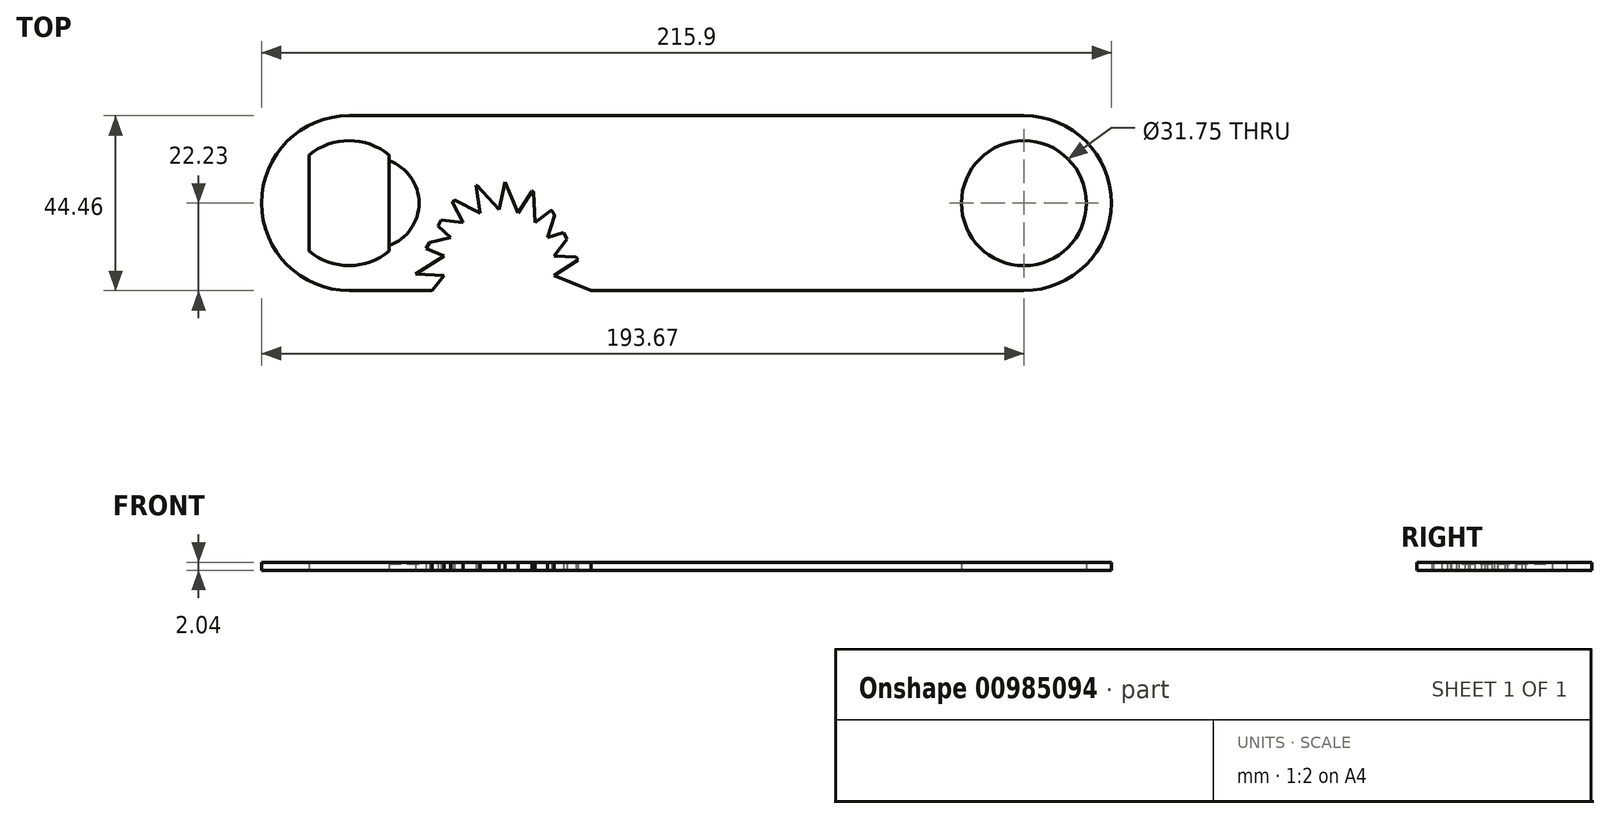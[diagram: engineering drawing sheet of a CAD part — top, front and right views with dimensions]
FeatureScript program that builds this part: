
annotation { "Feature Type Name" : "Feature", "Feature Type Description" : "" }
export const myFeature = defineFeature(function(context is Context, id is Id, definition is map)
    precondition{}
    {
        {
            var Q0;
            Q0=qCreatedBy(makeId("Top.planeOp"),FACE);
            var sketch = newSketch(context, id + "F0", { "sketchPlane" : qUnion([Q0])});
            skLineSegment(sketch, "E0.bottom", {"start": v(-95.25, 22.22) * mm, "end": v(76.2, 22.22) * mm});
            skLineSegment(sketch, "E0.top", {"start": v(-95.25, -22.23) * mm, "end": v(-77.64, -22.23) * mm});
            skArc(sketch, "E1", {"start": v(-95.25, 22.22) * mm, "mid": v(-117.48, 0) * mm, "end": v(-95.25, -22.23) * mm});
            skArc(sketch, "E2", {"start": v(76.2, -22.23) * mm, "mid": v(98.43, 0) * mm, "end": v(76.2, 22.22) * mm});
            skCircle(sketch, "E3", {"center": v(76.2, 0) * mm, "radius": 15.88 * mm});
            skArc(sketch, "E4", {"start": v(-85.1, 12.2) * mm, "mid": v(-95.25, 15.87) * mm, "end": v(-105.4, 12.2) * mm});
            skLineSegment(sketch, "E5", {"start": v(-105.41, -12.2) * mm, "end": v(-105.41, 12.2) * mm});
            skLineSegment(sketch, "E6", {"start": v(-85.1, -12.2) * mm, "end": v(-85.1, 12.2) * mm});
            skArc(sketch, "E7.trimOffspring", {"start": v(-105.41, -12.2) * mm, "mid": v(-95.25, -15.88) * mm, "end": v(-85.1, -12.2) * mm});
            skLineSegment(sketch, "E8", {"start": v(-77.64, -22.23) * mm, "end": v(-68.42, -4.5) * mm, "construction": true});
            skLineSegment(sketch, "E9", {"start": v(-48.23, 0) * mm, "end": v(-48.22, -0.02) * mm});
            skCircle(sketch, "E10", {"center": v(-57.15, -15.88) * mm, "radius": 15.24 * mm, "construction": true});
            skPoint(sketch, "E11.orphan", {"position": v(-57.15, 17.13) * mm});
            skLineSegment(sketch, "E12.trimOffspring", {"start": v(-36.66, -22.23) * mm, "end": v(76.2, -22.23) * mm});
            skLineSegment(sketch, "E13", {"start": v(-57.15, -0.64) * mm, "end": v(-57.15, 5.71) * mm, "construction": true});
            skLineSegment(sketch, "E14", {"start": v(-57.15, -1.65) * mm, "end": v(-64.4, 6.27) * mm});
            skLineSegment(sketch, "E15", {"start": v(-64.4, 6.27) * mm, "end": v(-54.83, 8.83) * mm});
            skLineSegment(sketch, "E16", {"start": v(-54.83, 8.83) * mm, "end": v(-57.15, -1.65) * mm});
            skLineSegment(sketch, "E17", {"start": v(-57.15, -1.65) * mm, "end": v(-59.62, 7.55) * mm, "construction": true});
            skLineSegment(sketch, "E18.1.0", {"start": v(-63.42, 8.14) * mm, "end": v(-62.01, -2.5) * mm});
            skLineSegment(sketch, "E18.1.1", {"start": v(-62.01, -2.5) * mm, "end": v(-71.54, 2.45) * mm});
            skLineSegment(sketch, "E18.1.2", {"start": v(-71.54, 2.45) * mm, "end": v(-63.42, 8.14) * mm});
            skLineSegment(sketch, "E18.2.0", {"start": v(-71.25, 4.55) * mm, "end": v(-66.3, -4.98) * mm});
            skLineSegment(sketch, "E18.2.1", {"start": v(-66.3, -4.98) * mm, "end": v(-76.94, -3.58) * mm});
            skLineSegment(sketch, "E18.2.2", {"start": v(-76.94, -3.58) * mm, "end": v(-71.25, 4.55) * mm});
            skLineSegment(sketch, "E18.3.0", {"start": v(-77.39, -1.5) * mm, "end": v(-69.47, -8.76) * mm});
            skLineSegment(sketch, "E18.3.1", {"start": v(-69.47, -8.76) * mm, "end": v(-79.95, -11.09) * mm});
            skLineSegment(sketch, "E18.3.2", {"start": v(-79.95, -11.09) * mm, "end": v(-77.39, -1.5) * mm});
            skLineSegment(sketch, "E18.4.0", {"start": v(-81.08, -9.3) * mm, "end": v(-71.16, -13.4) * mm});
            skLineSegment(sketch, "E18.4.1", {"start": v(-71.16, -13.4) * mm, "end": v(-80.21, -19.17) * mm});
            skLineSegment(sketch, "E18.4.2", {"start": v(-80.21, -19.17) * mm, "end": v(-81.08, -9.3) * mm});
            skLineSegment(sketch, "E18.5.0", {"start": v(-81.89, -17.88) * mm, "end": v(-71.16, -18.34) * mm});
            skLineSegment(sketch, "E18.5.1", {"start": v(-71.16, -18.34) * mm, "end": v(-74.14, -22.23) * mm});
            skLineSegment(sketch, "E18.5.2", {"start": v(-79.86, -22.23) * mm, "end": v(-81.89, -17.88) * mm});
            skLineSegment(sketch, "E19.2.13.0", {"start": v(-33.77, -22.23) * mm, "end": v(-43.14, -18.34) * mm});
            skLineSegment(sketch, "E19.3.13.0", {"start": v(-43.14, -18.34) * mm, "end": v(-34.09, -12.58) * mm});
            skLineSegment(sketch, "E19.6.13.0", {"start": v(-34.09, -12.58) * mm, "end": v(-33.24, -22.23) * mm});
            skLineSegment(sketch, "E19.2.14.0", {"start": v(-32.41, -13.87) * mm, "end": v(-43.14, -13.4) * mm});
            skLineSegment(sketch, "E19.3.14.0", {"start": v(-43.14, -13.4) * mm, "end": v(-36.6, -4.89) * mm});
            skLineSegment(sketch, "E19.6.14.0", {"start": v(-36.6, -4.89) * mm, "end": v(-32.41, -13.87) * mm});
            skLineSegment(sketch, "E19.2.15.0", {"start": v(-34.6, -5.53) * mm, "end": v(-44.83, -8.76) * mm});
            skLineSegment(sketch, "E19.3.15.0", {"start": v(-44.83, -8.76) * mm, "end": v(-41.6, 1.48) * mm});
            skLineSegment(sketch, "E19.6.15.0", {"start": v(-41.6, 1.48) * mm, "end": v(-34.6, -5.53) * mm});
            skLineSegment(sketch, "E19.2.16.0", {"start": v(-39.49, 1.56) * mm, "end": v(-48, -4.98) * mm});
            skLineSegment(sketch, "E19.3.16.0", {"start": v(-48, -4.98) * mm, "end": v(-48.48, 5.75) * mm});
            skLineSegment(sketch, "E19.6.16.0", {"start": v(-48.48, 5.75) * mm, "end": v(-39.49, 1.56) * mm});
            skLineSegment(sketch, "E19.2.17.0", {"start": v(-46.52, 6.55) * mm, "end": v(-52.29, -2.5) * mm});
            skLineSegment(sketch, "E19.3.17.0", {"start": v(-52.29, -2.5) * mm, "end": v(-56.4, 7.41) * mm});
            skLineSegment(sketch, "E19.6.17.0", {"start": v(-56.4, 7.41) * mm, "end": v(-46.52, 6.55) * mm});
            skLineSegment(sketch, "E20", {"start": v(-36.66, -22.23) * mm, "end": v(-33.77, -22.23) * mm});
            skPoint(sketch, "E21.orphan", {"position": v(-33.22, -22.45) * mm});
            skLineSegment(sketch, "E22", {"start": v(-74.14, -22.23) * mm, "end": v(-77.64, -22.23) * mm});
            skArc(sketch, "E23", {"start": v(-45.88, -4.5) * mm, "mid": v(-57.15, 2.33) * mm, "end": v(-68.42, -4.5) * mm, "construction": true});
            skLineSegment(sketch, "E24.trimOffspring", {"start": v(-66.23, -0.31) * mm, "end": v(-66.07, 0) * mm});
            skLineSegment(sketch, "E25.trimOffspring", {"start": v(-45.88, -4.5) * mm, "end": v(-36.66, -22.23) * mm, "construction": true});
            skLineSegment(sketch, "E26.0", {"start": v(-43.07, -3.04) * mm, "end": v(-33.08, -22.23) * mm});
            skArc(sketch, "E26.1", {"start": v(-43.07, -3.04) * mm, "mid": v(-57.15, 5.5) * mm, "end": v(-71.23, -3.04) * mm});
            skLineSegment(sketch, "E26.2", {"start": v(-81.22, -22.23) * mm, "end": v(-71.23, -3.04) * mm});
            skPoint(sketch, "E27", {"position": v(-117.48, 0) * mm});
            skCircle(sketch, "E28", {"center": v(-57.15, -15.88) * mm, "radius": 14.22 * mm, "construction": true});
            skSolve(sketch);
        }
        {
            var Q0;
            Q0=makeQuery(id+"F0.imprint","IMPRINT",FACE,{"disambiguationData":[TD([[makeQuery(id+"F0.imprint","IMPRINT",EDGE,{"derivedFrom":sQuery(id+"F0.wireOp",EDGE,"E0.bottom")}),-1.0]])]});
            var Q1;
            {var subQ0=sQuery(id+"F0.wireOp",EDGE,"E18.4.1");var subQ1=sQuery(id+"F0.wireOp",EDGE,"E8");var subQ2=makeQuery(id+"F0.imprint","INTERSECT",VERTEX,{"derivedFrom":[subQ1,subQ0]});Q1=makeQuery(id+"F0.imprint","IMPRINT",FACE,{"disambiguationData":[TD([[makeQuery(id+"F0.imprint","IMPRINT",EDGE,{"disambiguationData":[TD([[subQ2,-1.0]])],"derivedFrom":subQ1}),1.0]])]});}
            var Q2;
            {var subQ0=sQuery(id+"F0.wireOp",EDGE,"E18.5.0");var subQ1=sQuery(id+"F0.wireOp",EDGE,"E18.4.1");var subQ2=makeQuery(id+"F0.imprint","INTERSECT",VERTEX,{"derivedFrom":[subQ1,subQ0]});Q2=makeQuery(id+"F0.imprint","IMPRINT",FACE,{"disambiguationData":[TD([[makeQuery(id+"F0.imprint","IMPRINT",EDGE,{"disambiguationData":[TD([[subQ2,-1.0]])],"derivedFrom":subQ1}),-1.0]])]});}
            var Q3;
            {var subQ0=sQuery(id+"F0.wireOp",EDGE,"E18.3.1");var subQ1=sQuery(id+"F0.wireOp",EDGE,"E8");var subQ2=makeQuery(id+"F0.imprint","INTERSECT",VERTEX,{"derivedFrom":[subQ1,subQ0]});Q3=makeQuery(id+"F0.imprint","IMPRINT",FACE,{"disambiguationData":[TD([[makeQuery(id+"F0.imprint","IMPRINT",EDGE,{"disambiguationData":[TD([[subQ2,-1.0]])],"derivedFrom":subQ1}),1.0]])]});}
            var Q4;
            {var subQ0=sQuery(id+"F0.wireOp",EDGE,"E18.2.1");var subQ1=sQuery(id+"F0.wireOp",EDGE,"E8");var subQ2=makeQuery(id+"F0.imprint","INTERSECT",VERTEX,{"derivedFrom":[subQ1,subQ0]});Q4=makeQuery(id+"F0.imprint","IMPRINT",FACE,{"disambiguationData":[TD([[makeQuery(id+"F0.imprint","IMPRINT",EDGE,{"disambiguationData":[TD([[subQ2,-1.0]])],"derivedFrom":subQ1}),1.0]])]});}
            var Q5;
            {var subQ0=sQuery(id+"F0.wireOp",EDGE,"E18.3.0");var subQ1=sQuery(id+"F0.wireOp",EDGE,"E18.2.1");var subQ2=makeQuery(id+"F0.imprint","INTERSECT",VERTEX,{"derivedFrom":[subQ1,subQ0]});Q5=makeQuery(id+"F0.imprint","IMPRINT",FACE,{"disambiguationData":[TD([[makeQuery(id+"F0.imprint","IMPRINT",EDGE,{"disambiguationData":[TD([[subQ2,-1.0]])],"derivedFrom":subQ1}),-1.0]])]});}
            var Q6;
            {var subQ0=sQuery(id+"F0.wireOp",EDGE,"E18.2.0");var subQ1=sQuery(id+"F0.wireOp",EDGE,"E18.1.1");var subQ2=makeQuery(id+"F0.imprint","INTERSECT",VERTEX,{"derivedFrom":[subQ1,subQ0]});Q6=makeQuery(id+"F0.imprint","IMPRINT",FACE,{"disambiguationData":[TD([[makeQuery(id+"F0.imprint","IMPRINT",EDGE,{"disambiguationData":[TD([[subQ2,-1.0]])],"derivedFrom":subQ1}),-1.0]])]});}
            var Q7;
            {var subQ1=sQuery(id+"F0.wireOp",EDGE,"E18.1.1");var subQ7=sQuery(id+"F0.wireOp",EDGE,"PH1tnpYM-GYzg-ddA6-vLUi-DHPLtai6QRXg");var subQ8=makeQuery(id+"F0.imprint","INTERSECT",VERTEX,{"derivedFrom":[subQ7,subQ1]});Q7=makeQuery(id+"F0.imprint","IMPRINT",FACE,{"disambiguationData":[TD([[makeQuery(id+"F0.imprint","IMPRINT",EDGE,{"disambiguationData":[TD([[subQ8,1.0]])],"derivedFrom":subQ7}),-1.0]])]});}
            var Q8;
            {var subQ0=sQuery(id+"F0.wireOp",EDGE,"E18.1.1");var subQ1=sQuery(id+"F0.wireOp",EDGE,"PH1tnpYM-GYzg-ddA6-vLUi-DHPLtai6QRXg");var subQ2=makeQuery(id+"F0.imprint","INTERSECT",VERTEX,{"derivedFrom":[subQ1,subQ0]});Q8=makeQuery(id+"F0.imprint","IMPRINT",FACE,{"disambiguationData":[TD([[makeQuery(id+"F0.imprint","IMPRINT",EDGE,{"disambiguationData":[TD([[subQ2,1.0]])],"derivedFrom":subQ1}),1.0]])]});}
            var Q9;
            {var subQ0=sQuery(id+"F0.wireOp",EDGE,"E18.2.1");var subQ1=sQuery(id+"F0.wireOp",EDGE,"E8");var subQ2=makeQuery(id+"F0.imprint","INTERSECT",VERTEX,{"derivedFrom":[subQ1,subQ0]});Q9=makeQuery(id+"F0.imprint","IMPRINT",FACE,{"disambiguationData":[TD([[makeQuery(id+"F0.imprint","IMPRINT",EDGE,{"disambiguationData":[TD([[subQ2,-1.0]])],"derivedFrom":subQ1}),-1.0]])]});}
            var Q10;
            {var subQ0=sQuery(id+"F0.wireOp",EDGE,"E18.3.1");var subQ1=sQuery(id+"F0.wireOp",EDGE,"E8");var subQ2=makeQuery(id+"F0.imprint","INTERSECT",VERTEX,{"derivedFrom":[subQ1,subQ0]});Q10=makeQuery(id+"F0.imprint","IMPRINT",FACE,{"disambiguationData":[TD([[makeQuery(id+"F0.imprint","IMPRINT",EDGE,{"disambiguationData":[TD([[subQ2,-1.0]])],"derivedFrom":subQ1}),-1.0]])]});}
            var Q11;
            {var subQ0=sQuery(id+"F0.wireOp",EDGE,"E18.4.1");var subQ1=sQuery(id+"F0.wireOp",EDGE,"E8");var subQ2=makeQuery(id+"F0.imprint","INTERSECT",VERTEX,{"derivedFrom":[subQ1,subQ0]});Q11=makeQuery(id+"F0.imprint","IMPRINT",FACE,{"disambiguationData":[TD([[makeQuery(id+"F0.imprint","IMPRINT",EDGE,{"disambiguationData":[TD([[subQ2,-1.0]])],"derivedFrom":subQ1}),-1.0]])]});}
            var Q12;
            {var subQ0=sQuery(id+"F0.wireOp",EDGE,"E18.5.1");var subQ1=sQuery(id+"F0.wireOp",EDGE,"E8");var subQ2=makeQuery(id+"F0.imprint","INTERSECT",VERTEX,{"derivedFrom":[subQ1,subQ0]});Q12=makeQuery(id+"F0.imprint","IMPRINT",FACE,{"disambiguationData":[TD([[makeQuery(id+"F0.imprint","IMPRINT",EDGE,{"disambiguationData":[TD([[subQ2,-1.0]])],"derivedFrom":subQ1}),-1.0]])]});}
            var Q13;
            {var subQ0=sQuery(id+"F0.wireOp",EDGE,"E16");var subQ1=sQuery(id+"F0.wireOp",EDGE,"PH1tnpYM-GYzg-ddA6-vLUi-DHPLtai6QRXg");var subQ2=makeQuery(id+"F0.imprint","INTERSECT",VERTEX,{"derivedFrom":[subQ1,subQ0]});Q13=makeQuery(id+"F0.imprint","IMPRINT",FACE,{"disambiguationData":[TD([[makeQuery(id+"F0.imprint","IMPRINT",EDGE,{"disambiguationData":[TD([[subQ2,-1.0]])],"derivedFrom":subQ1}),1.0]])]});}
            var Q14;
            {var subQ0=sQuery(id+"F0.wireOp",EDGE,"E16");var subQ1=sQuery(id+"F0.wireOp",EDGE,"PH1tnpYM-GYzg-ddA6-vLUi-DHPLtai6QRXg");var subQ2=makeQuery(id+"F0.imprint","INTERSECT",VERTEX,{"derivedFrom":[subQ1,subQ0]});Q14=makeQuery(id+"F0.imprint","IMPRINT",FACE,{"disambiguationData":[TD([[makeQuery(id+"F0.imprint","IMPRINT",EDGE,{"disambiguationData":[TD([[subQ2,-1.0]])],"derivedFrom":subQ1}),-1.0]])]});}
            var Q15;
            {var subQ0=sQuery(id+"F0.wireOp",EDGE,"E18.1.0");var subQ1=sQuery(id+"F0.wireOp",EDGE,"PH1tnpYM-GYzg-ddA6-vLUi-DHPLtai6QRXg");var subQ2=makeQuery(id+"F0.imprint","INTERSECT",VERTEX,{"derivedFrom":[subQ1,subQ0]});Q15=makeQuery(id+"F0.imprint","IMPRINT",FACE,{"disambiguationData":[TD([[makeQuery(id+"F0.imprint","IMPRINT",EDGE,{"disambiguationData":[TD([[subQ2,-1.0]])],"derivedFrom":subQ1}),-1.0]])]});}
            var Q16;
            {var subQ0=sQuery(id+"F0.wireOp",EDGE,"E16");var subQ1=sQuery(id+"F0.wireOp",EDGE,"E15");var subQ2=makeQuery(id+"F0.imprint","INTERSECT",VERTEX,{"derivedFrom":[subQ1,subQ0]});Q16=makeQuery(id+"F0.imprint","IMPRINT",FACE,{"disambiguationData":[TD([[makeQuery(id+"F0.imprint","IMPRINT",EDGE,{"disambiguationData":[TD([[subQ2,1.0]])],"derivedFrom":subQ1}),-1.0]])]});}
            var Q17;
            {var subQ12=sQuery(id+"F0.wireOp",EDGE,"PH1tnpYM-GYzg-ddA6-vLUi-DHPLtai6QRXg");var subQ13=sQuery(id+"F0.wireOp",EDGE,"E9");var subQ14=makeQuery(id+"F0.imprint","INTERSECT",VERTEX,{"derivedFrom":[subQ13,subQ12]});Q17=makeQuery(id+"F0.imprint","IMPRINT",FACE,{"disambiguationData":[TD([[makeQuery(id+"F0.imprint","IMPRINT",EDGE,{"disambiguationData":[TD([[subQ14,-1.0]])],"derivedFrom":subQ13}),1.0]])]});}
            var Q18;
            {var subQ0=sQuery(id+"F0.wireOp",EDGE,"E19.2.17.0");var subQ1=sQuery(id+"F0.wireOp",EDGE,"E19.3.16.0");var subQ2=makeQuery(id+"F0.imprint","INTERSECT",VERTEX,{"derivedFrom":[subQ1,subQ0]});Q18=makeQuery(id+"F0.imprint","IMPRINT",FACE,{"disambiguationData":[TD([[makeQuery(id+"F0.imprint","IMPRINT",EDGE,{"disambiguationData":[TD([[subQ2,-1.0]])],"derivedFrom":subQ1}),-1.0]])]});}
            var Q19;
            {var subQ0=sQuery(id+"F0.wireOp",EDGE,"E19.3.15.0");var subQ1=sQuery(id+"F0.wireOp",EDGE,"E9");var subQ2=makeQuery(id+"F0.imprint","INTERSECT",VERTEX,{"derivedFrom":[subQ1,subQ0]});Q19=makeQuery(id+"F0.imprint","IMPRINT",FACE,{"disambiguationData":[TD([[makeQuery(id+"F0.imprint","IMPRINT",EDGE,{"disambiguationData":[TD([[subQ2,-1.0]])],"derivedFrom":subQ1}),1.0]])]});}
            var Q20;
            {var subQ0=sQuery(id+"F0.wireOp",EDGE,"E19.2.16.0");var subQ1=sQuery(id+"F0.wireOp",EDGE,"E19.3.15.0");var subQ2=makeQuery(id+"F0.imprint","INTERSECT",VERTEX,{"derivedFrom":[subQ1,subQ0]});Q20=makeQuery(id+"F0.imprint","IMPRINT",FACE,{"disambiguationData":[TD([[makeQuery(id+"F0.imprint","IMPRINT",EDGE,{"disambiguationData":[TD([[subQ2,-1.0]])],"derivedFrom":subQ1}),-1.0]])]});}
            var Q21;
            {var subQ0=sQuery(id+"F0.wireOp",EDGE,"E19.2.16.0");var subQ1=sQuery(id+"F0.wireOp",EDGE,"E9");var subQ2=makeQuery(id+"F0.imprint","INTERSECT",VERTEX,{"derivedFrom":[subQ1,subQ0]});Q21=makeQuery(id+"F0.imprint","IMPRINT",FACE,{"disambiguationData":[TD([[makeQuery(id+"F0.imprint","IMPRINT",EDGE,{"disambiguationData":[TD([[subQ2,-1.0]])],"derivedFrom":subQ1}),1.0]])]});}
            var Q22;
            {var subQ0=sQuery(id+"F0.wireOp",EDGE,"PH1tnpYM-GYzg-ddA6-vLUi-DHPLtai6QRXg");var subQ1=sQuery(id+"F0.wireOp",EDGE,"E9");var subQ2=makeQuery(id+"F0.imprint","INTERSECT",VERTEX,{"derivedFrom":[subQ1,subQ0]});Q22=makeQuery(id+"F0.imprint","IMPRINT",FACE,{"disambiguationData":[TD([[makeQuery(id+"F0.imprint","IMPRINT",EDGE,{"disambiguationData":[TD([[subQ2,-1.0]])],"derivedFrom":subQ1}),-1.0]])]});}
            var Q23;
            {var subQ0=sQuery(id+"F0.wireOp",EDGE,"E19.3.16.0");var subQ1=sQuery(id+"F0.wireOp",EDGE,"E9");var subQ2=makeQuery(id+"F0.imprint","INTERSECT",VERTEX,{"derivedFrom":[subQ1,subQ0]});Q23=makeQuery(id+"F0.imprint","IMPRINT",FACE,{"disambiguationData":[TD([[makeQuery(id+"F0.imprint","IMPRINT",EDGE,{"disambiguationData":[TD([[subQ2,-1.0]])],"derivedFrom":subQ1}),-1.0]])]});}
            var Q24;
            {var subQ0=sQuery(id+"F0.wireOp",EDGE,"E18.1.0");var subQ1=sQuery(id+"F0.wireOp",EDGE,"PH1tnpYM-GYzg-ddA6-vLUi-DHPLtai6QRXg");var subQ2=makeQuery(id+"F0.imprint","INTERSECT",VERTEX,{"derivedFrom":[subQ1,subQ0]});Q24=makeQuery(id+"F0.imprint","IMPRINT",FACE,{"disambiguationData":[TD([[makeQuery(id+"F0.imprint","IMPRINT",EDGE,{"disambiguationData":[TD([[subQ2,-1.0]])],"derivedFrom":subQ1}),1.0]])]});}
            var Q25;
            {var subQ0=sQuery(id+"F0.wireOp",EDGE,"E19.3.16.0");var subQ1=sQuery(id+"F0.wireOp",EDGE,"E9");var subQ2=makeQuery(id+"F0.imprint","INTERSECT",VERTEX,{"derivedFrom":[subQ1,subQ0]});Q25=makeQuery(id+"F0.imprint","IMPRINT",FACE,{"disambiguationData":[TD([[makeQuery(id+"F0.imprint","IMPRINT",EDGE,{"disambiguationData":[TD([[subQ2,-1.0]])],"derivedFrom":subQ1}),1.0]])]});}
            var Q26;
            {var subQ1=sQuery(id+"F0.wireOp",EDGE,"E9");var subQ7=sQuery(id+"F0.wireOp",EDGE,"E19.3.14.0");var subQ8=makeQuery(id+"F0.imprint","INTERSECT",VERTEX,{"derivedFrom":[subQ1,subQ7]});Q26=makeQuery(id+"F0.imprint","IMPRINT",FACE,{"disambiguationData":[TD([[makeQuery(id+"F0.imprint","IMPRINT",EDGE,{"disambiguationData":[TD([[subQ8,-1.0]])],"derivedFrom":subQ1}),1.0]])]});}
            var Q27;
            {var subQ0=sQuery(id+"F0.wireOp",EDGE,"E19.2.15.0");var subQ1=sQuery(id+"F0.wireOp",EDGE,"E19.3.14.0");var subQ2=makeQuery(id+"F0.imprint","INTERSECT",VERTEX,{"derivedFrom":[subQ1,subQ0]});Q27=makeQuery(id+"F0.imprint","IMPRINT",FACE,{"disambiguationData":[TD([[makeQuery(id+"F0.imprint","IMPRINT",EDGE,{"disambiguationData":[TD([[subQ2,-1.0]])],"derivedFrom":subQ1}),-1.0]])]});}
            var Q28;
            {var subQ0=sQuery(id+"F0.wireOp",EDGE,"E19.3.14.0");var subQ1=sQuery(id+"F0.wireOp",EDGE,"E9");var subQ2=makeQuery(id+"F0.imprint","INTERSECT",VERTEX,{"derivedFrom":[subQ1,subQ0]});Q28=makeQuery(id+"F0.imprint","IMPRINT",FACE,{"disambiguationData":[TD([[makeQuery(id+"F0.imprint","IMPRINT",EDGE,{"disambiguationData":[TD([[subQ2,-1.0]])],"derivedFrom":subQ1}),-1.0]])]});}
            var Q29;
            {var subQ0=sQuery(id+"F0.wireOp",EDGE,"E19.6.13.0");Q29=makeQuery(id+"F0.imprint","IMPRINT",FACE,{"disambiguationData":[TD([[makeQuery(id+"F0.imprint","IMPRINT",EDGE,{"derivedFrom":subQ0}),-1.0]])]});}
            var Q30;
            {var subQ0=sQuery(id+"F0.wireOp",EDGE,"E19.2.14.0");var subQ1=sQuery(id+"F0.wireOp",EDGE,"E9");var subQ2=makeQuery(id+"F0.imprint","INTERSECT",VERTEX,{"derivedFrom":[subQ1,subQ0]});Q30=makeQuery(id+"F0.imprint","IMPRINT",FACE,{"disambiguationData":[TD([[makeQuery(id+"F0.imprint","IMPRINT",EDGE,{"disambiguationData":[TD([[subQ2,-1.0]])],"derivedFrom":subQ1}),1.0]])]});}
            var Q31;
            {var subQ0=sQuery(id+"F0.wireOp",EDGE,"E19.2.14.0");var subQ1=sQuery(id+"F0.wireOp",EDGE,"E19.3.13.0");var subQ2=makeQuery(id+"F0.imprint","INTERSECT",VERTEX,{"derivedFrom":[subQ1,subQ0]});Q31=makeQuery(id+"F0.imprint","IMPRINT",FACE,{"disambiguationData":[TD([[makeQuery(id+"F0.imprint","IMPRINT",EDGE,{"disambiguationData":[TD([[subQ2,-1.0]])],"derivedFrom":subQ1}),-1.0]])]});}
            var Q32;
            {var subQ0=sQuery(id+"F0.wireOp",EDGE,"E19.3.15.0");var subQ1=sQuery(id+"F0.wireOp",EDGE,"E9");var subQ2=makeQuery(id+"F0.imprint","INTERSECT",VERTEX,{"derivedFrom":[subQ1,subQ0]});Q32=makeQuery(id+"F0.imprint","IMPRINT",FACE,{"disambiguationData":[TD([[makeQuery(id+"F0.imprint","IMPRINT",EDGE,{"disambiguationData":[TD([[subQ2,-1.0]])],"derivedFrom":subQ1}),-1.0]])]});}
            var Q33;
            {var subQ0=sQuery(id+"F0.wireOp",EDGE,"E19.2.15.0");var subQ1=sQuery(id+"F0.wireOp",EDGE,"E9");var subQ2=makeQuery(id+"F0.imprint","INTERSECT",VERTEX,{"derivedFrom":[subQ1,subQ0]});Q33=makeQuery(id+"F0.imprint","IMPRINT",FACE,{"disambiguationData":[TD([[makeQuery(id+"F0.imprint","IMPRINT",EDGE,{"disambiguationData":[TD([[subQ2,-1.0]])],"derivedFrom":subQ1}),1.0]])]});}
            var Q34;
            {var subQ0=sQuery(id+"F0.wireOp",EDGE,"PH1tnpYM-GYzg-ddA6-vLUi-DHPLtai6QRXg");var subQ1=sQuery(id+"F0.wireOp",EDGE,"E8");var subQ2=makeQuery(id+"F0.imprint","INTERSECT",VERTEX,{"derivedFrom":[subQ1,subQ0]});Q34=makeQuery(id+"F0.imprint","IMPRINT",FACE,{"disambiguationData":[TD([[makeQuery(id+"F0.imprint","IMPRINT",EDGE,{"disambiguationData":[TD([[subQ2,1.0]])],"derivedFrom":subQ1}),1.0]])]});}
            var Q35;
            {var subQ0=sQuery(id+"F0.wireOp",EDGE,"E18.3.0");var subQ1=sQuery(id+"F0.wireOp",EDGE,"E8");var subQ2=makeQuery(id+"F0.imprint","INTERSECT",VERTEX,{"derivedFrom":[subQ1,subQ0]});Q35=makeQuery(id+"F0.imprint","IMPRINT",FACE,{"disambiguationData":[TD([[makeQuery(id+"F0.imprint","IMPRINT",EDGE,{"disambiguationData":[TD([[subQ2,-1.0]])],"derivedFrom":subQ1}),1.0]])]});}
            var Q36;
            {var subQ0=sQuery(id+"F0.wireOp",EDGE,"E18.4.0");var subQ1=sQuery(id+"F0.wireOp",EDGE,"E8");var subQ2=makeQuery(id+"F0.imprint","INTERSECT",VERTEX,{"derivedFrom":[subQ1,subQ0]});Q36=makeQuery(id+"F0.imprint","IMPRINT",FACE,{"disambiguationData":[TD([[makeQuery(id+"F0.imprint","IMPRINT",EDGE,{"disambiguationData":[TD([[subQ2,-1.0]])],"derivedFrom":subQ1}),1.0]])]});}
            var Q37;
            {var subQ0=sQuery(id+"F0.wireOp",EDGE,"E18.5.0");var subQ1=sQuery(id+"F0.wireOp",EDGE,"E8");var subQ2=makeQuery(id+"F0.imprint","INTERSECT",VERTEX,{"derivedFrom":[subQ1,subQ0]});Q37=makeQuery(id+"F0.imprint","IMPRINT",FACE,{"disambiguationData":[TD([[makeQuery(id+"F0.imprint","IMPRINT",EDGE,{"disambiguationData":[TD([[subQ2,-1.0]])],"derivedFrom":subQ1}),1.0]])]});}
            var Q38;
            {var subQ0=sQuery(id+"F0.wireOp",EDGE,"E8");var subQ1=sQuery(id+"F0.wireOp",EDGE,"E0.top");var subQ2=makeQuery(id+"F0.imprint","INTERSECT",VERTEX,{"derivedFrom":[subQ1,subQ0]});Q38=makeQuery(id+"F0.imprint","IMPRINT",FACE,{"disambiguationData":[TD([[makeQuery(id+"F0.imprint","IMPRINT",EDGE,{"disambiguationData":[TD([[subQ2,1.0]])],"derivedFrom":subQ1}),1.0]])]});}
            var Q39;
            {var subQ0=sQuery(id+"F0.wireOp",EDGE,"E19.2.17.0");var subQ1=sQuery(id+"F0.wireOp",EDGE,"E9");var subQ2=makeQuery(id+"F0.imprint","INTERSECT",VERTEX,{"derivedFrom":[subQ1,subQ0]});Q39=makeQuery(id+"F0.imprint","IMPRINT",FACE,{"disambiguationData":[TD([[makeQuery(id+"F0.imprint","IMPRINT",EDGE,{"disambiguationData":[TD([[subQ2,-1.0]])],"derivedFrom":subQ1}),1.0]])]});}
            var Q40;
            {var subQ0=sQuery(id+"F0.wireOp",EDGE,"E19.3.17.0");var subQ1=sQuery(id+"F0.wireOp",EDGE,"PH1tnpYM-GYzg-ddA6-vLUi-DHPLtai6QRXg");var subQ2=makeQuery(id+"F0.imprint","INTERSECT",VERTEX,{"derivedFrom":[subQ1,subQ0]});Q40=makeQuery(id+"F0.imprint","IMPRINT",FACE,{"disambiguationData":[TD([[makeQuery(id+"F0.imprint","IMPRINT",EDGE,{"disambiguationData":[TD([[subQ2,-1.0]])],"derivedFrom":subQ1}),-1.0]])]});}
            var Q41;
            {var subQ0=sQuery(id+"F0.wireOp",EDGE,"E15");var subQ1=sQuery(id+"F0.wireOp",EDGE,"E14");var subQ2=makeQuery(id+"F0.imprint","INTERSECT",VERTEX,{"derivedFrom":[subQ1,subQ0]});Q41=makeQuery(id+"F0.imprint","IMPRINT",FACE,{"disambiguationData":[TD([[makeQuery(id+"F0.imprint","IMPRINT",EDGE,{"disambiguationData":[TD([[subQ2,1.0]])],"derivedFrom":subQ1}),-1.0]])]});}
            var Q42;
            {var subQ0=sQuery(id+"F0.wireOp",EDGE,"E19.2.17.0");var subQ1=sQuery(id+"F0.wireOp",EDGE,"PH1tnpYM-GYzg-ddA6-vLUi-DHPLtai6QRXg");var subQ2=makeQuery(id+"F0.imprint","INTERSECT",VERTEX,{"derivedFrom":[subQ1,subQ0]});Q42=makeQuery(id+"F0.imprint","IMPRINT",FACE,{"disambiguationData":[TD([[makeQuery(id+"F0.imprint","IMPRINT",EDGE,{"disambiguationData":[TD([[subQ2,-1.0]])],"derivedFrom":subQ1}),1.0]])]});}
            var Q43;
            {var subQ3=sQuery(id+"F0.wireOp",EDGE,"E19.2.17.0");var subQ6=sQuery(id+"F0.wireOp",EDGE,"PH1tnpYM-GYzg-ddA6-vLUi-DHPLtai6QRXg");var subQ12=makeQuery(id+"F0.imprint","INTERSECT",VERTEX,{"derivedFrom":[subQ6,subQ3]});Q43=makeQuery(id+"F0.imprint","IMPRINT",FACE,{"disambiguationData":[TD([[makeQuery(id+"F0.imprint","IMPRINT",EDGE,{"disambiguationData":[TD([[subQ12,-1.0]])],"derivedFrom":subQ6}),-1.0]])]});}
            var Q44;
            {var subQ0=sQuery(id+"F0.wireOp",EDGE,"E18.2.0");var subQ1=sQuery(id+"F0.wireOp",EDGE,"E8");var subQ2=makeQuery(id+"F0.imprint","INTERSECT",VERTEX,{"derivedFrom":[subQ1,subQ0]});Q44=makeQuery(id+"F0.imprint","IMPRINT",FACE,{"disambiguationData":[TD([[makeQuery(id+"F0.imprint","IMPRINT",EDGE,{"disambiguationData":[TD([[subQ2,-1.0]])],"derivedFrom":subQ1}),1.0]])]});}
            var Q45;
            {var subQ3=sQuery(id+"F0.wireOp",EDGE,"E9");var subQ7=sQuery(id+"F0.wireOp",EDGE,"E19.3.13.0");var subQ8=makeQuery(id+"F0.imprint","INTERSECT",VERTEX,{"derivedFrom":[subQ3,subQ7]});Q45=makeQuery(id+"F0.imprint","IMPRINT",FACE,{"disambiguationData":[TD([[makeQuery(id+"F0.imprint","IMPRINT",EDGE,{"disambiguationData":[TD([[subQ8,-1.0]])],"derivedFrom":subQ3}),1.0]])]});}
            var Q46;
            {var subQ0=sQuery(id+"F0.wireOp",EDGE,"E19.3.13.0");var subQ1=sQuery(id+"F0.wireOp",EDGE,"E9");var subQ2=makeQuery(id+"F0.imprint","INTERSECT",VERTEX,{"derivedFrom":[subQ1,subQ0]});Q46=makeQuery(id+"F0.imprint","IMPRINT",FACE,{"disambiguationData":[TD([[makeQuery(id+"F0.imprint","IMPRINT",EDGE,{"disambiguationData":[TD([[subQ2,-1.0]])],"derivedFrom":subQ1}),-1.0]])]});}
            var Q47;
            {var subQ0=sQuery(id+"F0.wireOp",EDGE,"E14");var subQ1=sQuery(id+"F0.wireOp",EDGE,"PH1tnpYM-GYzg-ddA6-vLUi-DHPLtai6QRXg");var subQ2=makeQuery(id+"F0.imprint","INTERSECT",VERTEX,{"derivedFrom":[subQ1,subQ0]});Q47=makeQuery(id+"F0.imprint","IMPRINT",FACE,{"disambiguationData":[TD([[makeQuery(id+"F0.imprint","IMPRINT",EDGE,{"disambiguationData":[TD([[subQ2,1.0]])],"derivedFrom":subQ1}),1.0]])]});}
            var Q48;
            {var subQ0=sQuery(id+"F0.wireOp",EDGE,"E19.6.17.0");var subQ1=sQuery(id+"F0.wireOp",EDGE,"E16");var subQ2=makeQuery(id+"F0.imprint","INTERSECT",VERTEX,{"derivedFrom":[subQ1,subQ0]});Q48=makeQuery(id+"F0.imprint","IMPRINT",FACE,{"disambiguationData":[TD([[makeQuery(id+"F0.imprint","IMPRINT",EDGE,{"disambiguationData":[TD([[subQ2,-1.0]])],"derivedFrom":subQ1}),-1.0]])]});}
            var Q49;
            {var subQ0=sQuery(id+"F0.wireOp",EDGE,"E16");var subQ1=sQuery(id+"F0.wireOp",EDGE,"E14");var subQ2=makeQuery(id+"F0.imprint","INTERSECT",VERTEX,{"derivedFrom":[subQ1,subQ0]});Q49=makeQuery(id+"F0.imprint","IMPRINT",FACE,{"disambiguationData":[TD([[makeQuery(id+"F0.imprint","IMPRINT",EDGE,{"disambiguationData":[TD([[subQ2,-1.0]])],"derivedFrom":subQ1}),-1.0]])]});}
            var Q50;
            {var subQ0=sQuery(id+"F0.wireOp",EDGE,"E18.1.1");var subQ1=sQuery(id+"F0.wireOp",EDGE,"E18.1.0");var subQ2=makeQuery(id+"F0.imprint","INTERSECT",VERTEX,{"derivedFrom":[subQ1,subQ0]});Q50=makeQuery(id+"F0.imprint","IMPRINT",FACE,{"disambiguationData":[TD([[makeQuery(id+"F0.imprint","IMPRINT",EDGE,{"disambiguationData":[TD([[subQ2,1.0]])],"derivedFrom":subQ1}),-1.0]])]});}
            var Q51;
            {var subQ0=sQuery(id+"F0.wireOp",EDGE,"E18.2.0");var subQ1=sQuery(id+"F0.wireOp",EDGE,"E8");var subQ2=makeQuery(id+"F0.imprint","INTERSECT",VERTEX,{"derivedFrom":[subQ1,subQ0]});Q51=makeQuery(id+"F0.imprint","IMPRINT",FACE,{"disambiguationData":[TD([[makeQuery(id+"F0.imprint","IMPRINT",EDGE,{"disambiguationData":[TD([[subQ2,-1.0]])],"derivedFrom":subQ1}),-1.0]])]});}
            var Q52;
            {var subQ0=sQuery(id+"F0.wireOp",EDGE,"E19.3.17.0");var subQ1=sQuery(id+"F0.wireOp",EDGE,"E19.2.17.0");var subQ2=makeQuery(id+"F0.imprint","INTERSECT",VERTEX,{"derivedFrom":[subQ1,subQ0]});Q52=makeQuery(id+"F0.imprint","IMPRINT",FACE,{"disambiguationData":[TD([[makeQuery(id+"F0.imprint","IMPRINT",EDGE,{"disambiguationData":[TD([[subQ2,1.0]])],"derivedFrom":subQ1}),-1.0]])]});}
            var Q53;
            {var subQ0=sQuery(id+"F0.wireOp",EDGE,"E19.3.16.0");var subQ1=sQuery(id+"F0.wireOp",EDGE,"E19.2.16.0");var subQ2=makeQuery(id+"F0.imprint","INTERSECT",VERTEX,{"derivedFrom":[subQ1,subQ0]});Q53=makeQuery(id+"F0.imprint","IMPRINT",FACE,{"disambiguationData":[TD([[makeQuery(id+"F0.imprint","IMPRINT",EDGE,{"disambiguationData":[TD([[subQ2,1.0]])],"derivedFrom":subQ1}),-1.0]])]});}
            var Q54;
            {var subQ3=sQuery(id+"F0.wireOp",EDGE,"E18.3.2");var subQ5=sQuery(id+"F0.wireOp",EDGE,"E18.3.1");var subQ6=makeQuery(id+"F0.imprint","INTERSECT",VERTEX,{"derivedFrom":[subQ5,subQ3]});Q54=makeQuery(id+"F0.imprint","IMPRINT",FACE,{"disambiguationData":[TD([[makeQuery(id+"F0.imprint","IMPRINT",EDGE,{"disambiguationData":[TD([[subQ6,1.0]])],"derivedFrom":subQ5}),1.0]])]});}
            var Q55;
            {var subQ0=sQuery(id+"F0.wireOp",EDGE,"E18.3.2");var subQ1=sQuery(id+"F0.wireOp",EDGE,"E18.3.1");var subQ2=makeQuery(id+"F0.imprint","INTERSECT",VERTEX,{"derivedFrom":[subQ1,subQ0]});Q55=makeQuery(id+"F0.imprint","IMPRINT",FACE,{"disambiguationData":[TD([[makeQuery(id+"F0.imprint","IMPRINT",EDGE,{"disambiguationData":[TD([[subQ2,1.0]])],"derivedFrom":subQ1}),-1.0]])]});}
            var Q56;
            {var subQ5=sQuery(id+"F0.wireOp",EDGE,"E18.4.2");var subQ7=sQuery(id+"F0.wireOp",EDGE,"E18.4.1");var subQ8=makeQuery(id+"F0.imprint","INTERSECT",VERTEX,{"derivedFrom":[subQ7,subQ5]});Q56=makeQuery(id+"F0.imprint","IMPRINT",FACE,{"disambiguationData":[TD([[makeQuery(id+"F0.imprint","IMPRINT",EDGE,{"disambiguationData":[TD([[subQ8,1.0]])],"derivedFrom":subQ7}),1.0]])]});}
            var Q57;
            {var subQ0=sQuery(id+"F0.wireOp",EDGE,"E18.4.2");var subQ1=sQuery(id+"F0.wireOp",EDGE,"E18.4.1");var subQ2=makeQuery(id+"F0.imprint","INTERSECT",VERTEX,{"derivedFrom":[subQ1,subQ0]});Q57=makeQuery(id+"F0.imprint","IMPRINT",FACE,{"disambiguationData":[TD([[makeQuery(id+"F0.imprint","IMPRINT",EDGE,{"disambiguationData":[TD([[subQ2,1.0]])],"derivedFrom":subQ1}),-1.0]])]});}
            var Q58;
            {var subQ0=sQuery(id+"F0.wireOp",EDGE,"E18.4.1");var subQ1=sQuery(id+"F0.wireOp",EDGE,"E18.4.0");var subQ2=makeQuery(id+"F0.imprint","INTERSECT",VERTEX,{"derivedFrom":[subQ1,subQ0]});Q58=makeQuery(id+"F0.imprint","IMPRINT",FACE,{"disambiguationData":[TD([[makeQuery(id+"F0.imprint","IMPRINT",EDGE,{"disambiguationData":[TD([[subQ2,1.0]])],"derivedFrom":subQ1}),-1.0]])]});}
            var Q59;
            {var subQ0=sQuery(id+"F0.wireOp",EDGE,"E18.3.1");var subQ1=sQuery(id+"F0.wireOp",EDGE,"E18.3.0");var subQ2=makeQuery(id+"F0.imprint","INTERSECT",VERTEX,{"derivedFrom":[subQ1,subQ0]});Q59=makeQuery(id+"F0.imprint","IMPRINT",FACE,{"disambiguationData":[TD([[makeQuery(id+"F0.imprint","IMPRINT",EDGE,{"disambiguationData":[TD([[subQ2,1.0]])],"derivedFrom":subQ1}),-1.0]])]});}
            var Q60;
            {var subQ3=sQuery(id+"F0.wireOp",EDGE,"E18.2.2");var subQ5=sQuery(id+"F0.wireOp",EDGE,"E18.2.1");var subQ6=makeQuery(id+"F0.imprint","INTERSECT",VERTEX,{"derivedFrom":[subQ5,subQ3]});Q60=makeQuery(id+"F0.imprint","IMPRINT",FACE,{"disambiguationData":[TD([[makeQuery(id+"F0.imprint","IMPRINT",EDGE,{"disambiguationData":[TD([[subQ6,1.0]])],"derivedFrom":subQ5}),1.0]])]});}
            var Q61;
            {var subQ3=sQuery(id+"F0.wireOp",EDGE,"E18.1.2");var subQ5=sQuery(id+"F0.wireOp",EDGE,"E18.1.1");var subQ6=makeQuery(id+"F0.imprint","INTERSECT",VERTEX,{"derivedFrom":[subQ5,subQ3]});Q61=makeQuery(id+"F0.imprint","IMPRINT",FACE,{"disambiguationData":[TD([[makeQuery(id+"F0.imprint","IMPRINT",EDGE,{"disambiguationData":[TD([[subQ6,1.0]])],"derivedFrom":subQ5}),1.0]])]});}
            var Q62;
            {var subQ0=sQuery(id+"F0.wireOp",EDGE,"E18.2.1");var subQ1=sQuery(id+"F0.wireOp",EDGE,"E18.2.0");var subQ2=makeQuery(id+"F0.imprint","INTERSECT",VERTEX,{"derivedFrom":[subQ1,subQ0]});Q62=makeQuery(id+"F0.imprint","IMPRINT",FACE,{"disambiguationData":[TD([[makeQuery(id+"F0.imprint","IMPRINT",EDGE,{"disambiguationData":[TD([[subQ2,1.0]])],"derivedFrom":subQ1}),-1.0]])]});}
            var Q63;
            {var subQ3=sQuery(id+"F0.wireOp",EDGE,"E14");var subQ7=sQuery(id+"F0.wireOp",EDGE,"E15");var subQ13=makeQuery(id+"F0.imprint","INTERSECT",VERTEX,{"derivedFrom":[subQ3,subQ7]});Q63=makeQuery(id+"F0.imprint","IMPRINT",FACE,{"disambiguationData":[TD([[makeQuery(id+"F0.imprint","IMPRINT",EDGE,{"disambiguationData":[TD([[subQ13,1.0]])],"derivedFrom":subQ3}),1.0]])]});}
            var Q64;
            {var subQ0=sQuery(id+"F0.wireOp",EDGE,"E19.6.17.0");var subQ8=sQuery(id+"F0.wireOp",EDGE,"E16");var subQ9=makeQuery(id+"F0.imprint","INTERSECT",VERTEX,{"derivedFrom":[subQ8,subQ0]});Q64=makeQuery(id+"F0.imprint","IMPRINT",FACE,{"disambiguationData":[TD([[makeQuery(id+"F0.imprint","IMPRINT",EDGE,{"disambiguationData":[TD([[subQ9,-1.0]])],"derivedFrom":subQ8}),1.0]])]});}
            var Q65;
            {var subQ3=sQuery(id+"F0.wireOp",EDGE,"E19.6.15.0");var subQ9=sQuery(id+"F0.wireOp",EDGE,"E19.3.15.0");var subQ10=makeQuery(id+"F0.imprint","INTERSECT",VERTEX,{"derivedFrom":[subQ9,subQ3]});Q65=makeQuery(id+"F0.imprint","IMPRINT",FACE,{"disambiguationData":[TD([[makeQuery(id+"F0.imprint","IMPRINT",EDGE,{"disambiguationData":[TD([[subQ10,1.0]])],"derivedFrom":subQ9}),1.0]])]});}
            var Q66;
            {var subQ3=sQuery(id+"F0.wireOp",EDGE,"E19.6.14.0");var subQ5=sQuery(id+"F0.wireOp",EDGE,"E19.3.14.0");var subQ6=makeQuery(id+"F0.imprint","INTERSECT",VERTEX,{"derivedFrom":[subQ5,subQ3]});Q66=makeQuery(id+"F0.imprint","IMPRINT",FACE,{"disambiguationData":[TD([[makeQuery(id+"F0.imprint","IMPRINT",EDGE,{"disambiguationData":[TD([[subQ6,1.0]])],"derivedFrom":subQ5}),1.0]])]});}
            var Q67;
            {var subQ3=sQuery(id+"F0.wireOp",EDGE,"E19.6.13.0");var subQ7=sQuery(id+"F0.wireOp",EDGE,"E19.3.13.0");var subQ9=makeQuery(id+"F0.imprint","INTERSECT",VERTEX,{"derivedFrom":[subQ7,subQ3]});Q67=makeQuery(id+"F0.imprint","IMPRINT",FACE,{"disambiguationData":[TD([[makeQuery(id+"F0.imprint","IMPRINT",EDGE,{"disambiguationData":[TD([[subQ9,1.0]])],"derivedFrom":subQ7}),1.0]])]});}
            var Q68;
            {var subQ0=sQuery(id+"F0.wireOp",EDGE,"E26.0");var subQ1=sQuery(id+"F0.wireOp",EDGE,"E19.3.13.0");var subQ2=makeQuery(id+"F0.imprint","INTERSECT",VERTEX,{"derivedFrom":[subQ1,subQ0]});Q68=makeQuery(id+"F0.imprint","IMPRINT",FACE,{"disambiguationData":[TD([[makeQuery(id+"F0.imprint","IMPRINT",EDGE,{"disambiguationData":[TD([[subQ2,-1.0]])],"derivedFrom":subQ1}),-1.0]])]});}
            var Q69;
            {var subQ7=sQuery(id+"F0.wireOp",EDGE,"E19.2.13.0");Q69=makeQuery(id+"F0.imprint","IMPRINT",FACE,{"disambiguationData":[TD([[makeQuery(id+"F0.imprint","IMPRINT",EDGE,{"derivedFrom":subQ7}),-1.0]])]});}
            var Q70;
            {var subQ0=sQuery(id+"F0.wireOp",EDGE,"E19.3.14.0");var subQ1=sQuery(id+"F0.wireOp",EDGE,"E19.2.14.0");var subQ2=makeQuery(id+"F0.imprint","INTERSECT",VERTEX,{"derivedFrom":[subQ1,subQ0]});Q70=makeQuery(id+"F0.imprint","IMPRINT",FACE,{"disambiguationData":[TD([[makeQuery(id+"F0.imprint","IMPRINT",EDGE,{"disambiguationData":[TD([[subQ2,1.0]])],"derivedFrom":subQ1}),-1.0]])]});}
            var Q71;
            {var subQ0=sQuery(id+"F0.wireOp",EDGE,"E19.3.15.0");var subQ1=sQuery(id+"F0.wireOp",EDGE,"E19.2.15.0");var subQ2=makeQuery(id+"F0.imprint","INTERSECT",VERTEX,{"derivedFrom":[subQ1,subQ0]});Q71=makeQuery(id+"F0.imprint","IMPRINT",FACE,{"disambiguationData":[TD([[makeQuery(id+"F0.imprint","IMPRINT",EDGE,{"disambiguationData":[TD([[subQ2,1.0]])],"derivedFrom":subQ1}),-1.0]])]});}
            var Q72;
            {var subQ0=sQuery(id+"F0.wireOp",EDGE,"E26.2");var subQ1=sQuery(id+"F0.wireOp",EDGE,"E18.2.1");var subQ2=makeQuery(id+"F0.imprint","INTERSECT",VERTEX,{"derivedFrom":[subQ1,subQ0]});Q72=makeQuery(id+"F0.imprint","IMPRINT",FACE,{"disambiguationData":[TD([[makeQuery(id+"F0.imprint","IMPRINT",EDGE,{"disambiguationData":[TD([[subQ2,-1.0]])],"derivedFrom":subQ1}),1.0]])]});}
            var Q73;
            {var subQ0=sQuery(id+"F0.wireOp",EDGE,"E26.2");var subQ1=sQuery(id+"F0.wireOp",EDGE,"E18.3.1");var subQ2=makeQuery(id+"F0.imprint","INTERSECT",VERTEX,{"derivedFrom":[subQ1,subQ0]});Q73=makeQuery(id+"F0.imprint","IMPRINT",FACE,{"disambiguationData":[TD([[makeQuery(id+"F0.imprint","IMPRINT",EDGE,{"disambiguationData":[TD([[subQ2,-1.0]])],"derivedFrom":subQ1}),1.0]])]});}
            var Q74;
            {var subQ0=sQuery(id+"F0.wireOp",EDGE,"E26.1");var subQ1=sQuery(id+"F0.wireOp",EDGE,"E18.1.1");var subQ2=makeQuery(id+"F0.imprint","INTERSECT",VERTEX,{"derivedFrom":[subQ1,subQ0]});Q74=makeQuery(id+"F0.imprint","IMPRINT",FACE,{"disambiguationData":[TD([[makeQuery(id+"F0.imprint","IMPRINT",EDGE,{"disambiguationData":[TD([[subQ2,-1.0]])],"derivedFrom":subQ1}),1.0]])]});}
            var Q75;
            {var subQ0=sQuery(id+"F0.wireOp",EDGE,"E26.1");var subQ1=sQuery(id+"F0.wireOp",EDGE,"E19.3.16.0");var subQ2=makeQuery(id+"F0.imprint","INTERSECT",VERTEX,{"derivedFrom":[subQ1,subQ0]});Q75=makeQuery(id+"F0.imprint","IMPRINT",FACE,{"disambiguationData":[TD([[makeQuery(id+"F0.imprint","IMPRINT",EDGE,{"disambiguationData":[TD([[subQ2,-1.0]])],"derivedFrom":subQ1}),1.0]])]});}
            var Q76;
            {var subQ0=sQuery(id+"F0.wireOp",EDGE,"E26.0");var subQ1=sQuery(id+"F0.wireOp",EDGE,"E19.3.15.0");var subQ2=makeQuery(id+"F0.imprint","INTERSECT",VERTEX,{"derivedFrom":[subQ1,subQ0]});Q76=makeQuery(id+"F0.imprint","IMPRINT",FACE,{"disambiguationData":[TD([[makeQuery(id+"F0.imprint","IMPRINT",EDGE,{"disambiguationData":[TD([[subQ2,-1.0]])],"derivedFrom":subQ1}),1.0]])]});}
            var Q77;
            {var subQ0=sQuery(id+"F0.wireOp",EDGE,"E26.0");var subQ1=sQuery(id+"F0.wireOp",EDGE,"E19.3.14.0");var subQ2=makeQuery(id+"F0.imprint","INTERSECT",VERTEX,{"derivedFrom":[subQ1,subQ0]});Q77=makeQuery(id+"F0.imprint","IMPRINT",FACE,{"disambiguationData":[TD([[makeQuery(id+"F0.imprint","IMPRINT",EDGE,{"disambiguationData":[TD([[subQ2,-1.0]])],"derivedFrom":subQ1}),1.0]])]});}
            var Q78;
            {var subQ0=sQuery(id+"F0.wireOp",EDGE,"E26.0");var subQ1=sQuery(id+"F0.wireOp",EDGE,"E19.3.13.0");var subQ2=makeQuery(id+"F0.imprint","INTERSECT",VERTEX,{"derivedFrom":[subQ1,subQ0]});Q78=makeQuery(id+"F0.imprint","IMPRINT",FACE,{"disambiguationData":[TD([[makeQuery(id+"F0.imprint","IMPRINT",EDGE,{"disambiguationData":[TD([[subQ2,-1.0]])],"derivedFrom":subQ1}),1.0]])]});}
            var Q79;
            {var subQ0=sQuery(id+"F0.wireOp",EDGE,"E26.1");var subQ1=sQuery(id+"F0.wireOp",EDGE,"E16");var subQ2=makeQuery(id+"F0.imprint","INTERSECT",VERTEX,{"derivedFrom":[subQ1,subQ0]});Q79=makeQuery(id+"F0.imprint","IMPRINT",FACE,{"disambiguationData":[TD([[makeQuery(id+"F0.imprint","IMPRINT",EDGE,{"disambiguationData":[TD([[subQ2,1.0]])],"derivedFrom":subQ1}),1.0]])]});}
            var Q80;
            {var subQ0=sQuery(id+"F0.wireOp",EDGE,"E26.1");var subQ1=sQuery(id+"F0.wireOp",EDGE,"E14");var subQ2=makeQuery(id+"F0.imprint","INTERSECT",VERTEX,{"derivedFrom":[subQ1,subQ0]});Q80=makeQuery(id+"F0.imprint","IMPRINT",FACE,{"disambiguationData":[TD([[makeQuery(id+"F0.imprint","IMPRINT",EDGE,{"disambiguationData":[TD([[subQ2,-1.0]])],"derivedFrom":subQ1}),1.0]])]});}
            var Q81;
            {var subQ0=sQuery(id+"F0.wireOp",EDGE,"E19.6.13.0");var subQ1=sQuery(id+"F0.wireOp",EDGE,"E12.trimOffspring");var subQ2=makeQuery(id+"F0.imprint","INTERSECT",VERTEX,{"derivedFrom":[subQ1,subQ0]});Q81=makeQuery(id+"F0.imprint","IMPRINT",FACE,{"disambiguationData":[TD([[makeQuery(id+"F0.imprint","IMPRINT",EDGE,{"disambiguationData":[TD([[subQ2,-1.0]])],"derivedFrom":subQ1}),1.0]])]});}
            var Q82;
            {var subQ0=sQuery(id+"F0.wireOp",EDGE,"E18.5.1");Q82=makeQuery(id+"F0.imprint","IMPRINT",FACE,{"disambiguationData":[TD([[makeQuery(id+"F0.imprint","IMPRINT",EDGE,{"derivedFrom":subQ0}),-1.0]])]});}
            extrude(context, id + "F1", {"entities" : qUnion([Q0, Q1, Q2, Q3, Q4, Q5, Q6, Q7, Q8, Q9, Q10, Q11, Q12, Q13, Q14, Q15, Q16, Q17, Q18, Q19, Q20, Q21, Q22, Q23, Q24, Q25, Q26, Q27, Q28, Q29, Q30, Q31, Q32, Q33, Q34, Q35, Q36, Q37, Q38, Q39, Q40, Q41, Q42, Q43, Q44, Q45, Q46, Q47, Q48, Q49, Q50, Q51, Q52, Q53, Q54, Q55, Q56, Q57, Q58, Q59, Q60, Q61, Q62, Q63, Q64, Q65, Q66, Q67, Q68, Q69, Q70, Q71, Q72, Q73, Q74, Q75, Q76, Q77, Q78, Q79, Q80, Q81, Q82]), "endBound" : BoundingType.SYMMETRIC, "depth" : 2.03 * mm, "offsetDistance" : 25.4 * mm});
        }
        {
            var Q0;
            Q0=makeQuery(id+"F1.opExtrude","CAP_FACE",FACE,{"disambiguationData":[OSD([sQuery(id+"F0.wireOp",EDGE,"E0.bottom"),sQuery(id+"F0.wireOp",EDGE,"E0.top"),sQuery(id+"F0.wireOp",EDGE,"E1"),sQuery(id+"F0.wireOp",EDGE,"E2"),sQuery(id+"F0.wireOp",EDGE,"E3"),sQuery(id+"F0.wireOp",EDGE,"E4"),sQuery(id+"F0.wireOp",EDGE,"E5"),sQuery(id+"F0.wireOp",EDGE,"E6"),sQuery(id+"F0.wireOp",EDGE,"E7.trimOffspring"),sQuery(id+"F0.wireOp",EDGE,"E12.trimOffspring"),sQuery(id+"F0.wireOp",EDGE,"E14"),sQuery(id+"F0.wireOp",EDGE,"E16"),sQuery(id+"F0.wireOp",EDGE,"E18.1.0"),sQuery(id+"F0.wireOp",EDGE,"E18.1.1"),sQuery(id+"F0.wireOp",EDGE,"E18.2.0"),sQuery(id+"F0.wireOp",EDGE,"E18.2.1"),sQuery(id+"F0.wireOp",EDGE,"E18.3.0"),sQuery(id+"F0.wireOp",EDGE,"E18.3.1"),sQuery(id+"F0.wireOp",EDGE,"E18.4.0"),sQuery(id+"F0.wireOp",EDGE,"E18.4.1"),sQuery(id+"F0.wireOp",EDGE,"E18.5.0"),sQuery(id+"F0.wireOp",EDGE,"E18.5.1"),sQuery(id+"F0.wireOp",EDGE,"E19.2.13.0"),sQuery(id+"F0.wireOp",EDGE,"E19.3.13.0"),sQuery(id+"F0.wireOp",EDGE,"E19.6.13.0"),sQuery(id+"F0.wireOp",EDGE,"E19.2.14.0"),sQuery(id+"F0.wireOp",EDGE,"E19.3.14.0"),sQuery(id+"F0.wireOp",EDGE,"E19.2.15.0"),sQuery(id+"F0.wireOp",EDGE,"E19.3.15.0"),sQuery(id+"F0.wireOp",EDGE,"E19.2.16.0"),sQuery(id+"F0.wireOp",EDGE,"E19.3.16.0"),sQuery(id+"F0.wireOp",EDGE,"E19.2.17.0"),sQuery(id+"F0.wireOp",EDGE,"E19.3.17.0"),sQuery(id+"F0.wireOp",EDGE,"E22"),sQuery(id+"F0.wireOp",EDGE,"E26.0"),sQuery(id+"F0.wireOp",EDGE,"E26.1"),sQuery(id+"F0.wireOp",EDGE,"E26.2")])],"isStart":false});
            var sketch = newSketch(context, id + "F2", { "sketchPlane" : qUnion([Q0])});
            skCircle(sketch, "E29", {"center": v(-88.9, 0) * mm, "radius": 11.43 * mm});
            skSolve(sketch);
        }
        {
            var Q0;
            {var subQ0=sQuery(id+"F2.wireOp",EDGE,"E29");var subQ1=makeQuery(id+"F1.opExtrude","CAP_EDGE",EDGE,{"disambiguationData":[OSD([sQuery(id+"F0.wireOp",EDGE,"E6")])],"isStart":false});var subQ2=makeQuery(id+"F2.imprint","INTERSECT",VERTEX,{"disambiguationData":[OD(0.0)],"derivedFrom":[subQ1,subQ0]});Q0=makeQuery(id+"F2.imprint","IMPRINT",FACE,{"disambiguationData":[TD([[makeQuery(id+"F2.imprint","IMPRINT",EDGE,{"disambiguationData":[TD([[subQ2,1.0]])],"derivedFrom":subQ0}),1.0]])]});}
            extrude(context, id + "F3", {"entities" : qUnion([Q0]), "operationType" : NewBodyOperationType.REMOVE, "oppositeDirection" : true, "depth" : 0.38 * mm, "offsetDistance" : 25.4 * mm});
        }
    });
